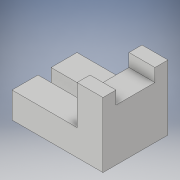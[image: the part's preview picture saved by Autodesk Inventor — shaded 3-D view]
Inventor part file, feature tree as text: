
AUTODESK INVENTOR PART (.ipt)
format: ipt  version: 2018 (Build 220112000, 112)  size: 122,368 bytes
history: native  units: in
note: dims shown in document units (in); Inventor stores cm internally (conversion verified against a paired STEP export)
features: extrude x4, sketch x4
ambient origin geometry x8: Origin, YZ Plane, XZ Plane, XY Plane, X Axis, Y Axis, Z Axis, Center Point
bodies: Solid1 (feature_tree)
feature tree (8):
  extrude  "Extrusion1"  Depth=2.5in
  extrude  "Extrusion2"  Depth=1.0in
  extrude  "Extrusion3"  Depth=0.5in
  extrude  "Extrusion4"  Depth=1.0in
  sketch  "Sketch1"  dims[d0=3.5in d1=2.5in]
  sketch  "Sketch2"  dims[d2=1.0in d3=0.0in d4=1.0in]
  sketch  "Sketch3"  dims[d5=1.5in d6=0.5in]
  sketch  "Sketch4"  dims[d7=1.0in d8=0.0in d9=1.0in d10=1.5in d11=0.0in d12=0.5in d13=1.5in d14=0.5in d15=0.0in]
